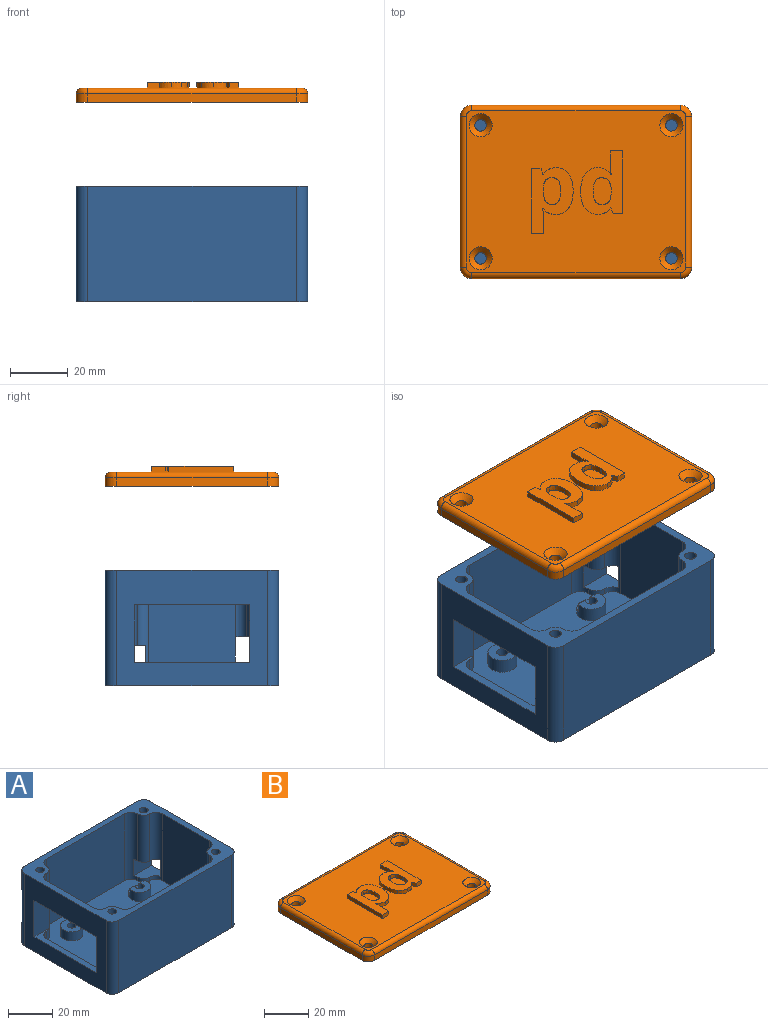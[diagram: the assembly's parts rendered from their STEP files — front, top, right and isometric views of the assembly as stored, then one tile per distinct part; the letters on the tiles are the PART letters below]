
ASSEMBLY  parts=2 mates=1
PART A: 74 faces, bbox 80x60x40 mm
  f0: plane 30x12mm, normal (1,0,0), area 360mm2, adj f3,f5,f16,f66
  f1: plane 52x40mm, normal (-1,0,0), area 1280mm2, adj f16,f19,f66,f67,f68,f69,f70,f71
  f2: cylinder r=4mm len=37mm, axis (0,0,1), area 174.7mm2, adj f5,f11,f16,f27,f33,f66,f67,f68
  f3: cylinder r=4mm len=12mm, axis (0,0,-1), area 75.4mm2, adj f0,f4,f16,f66
  f4: cylinder r=4mm len=37mm, axis (0,0,1), area 174.7mm2, adj f3,f11,f16,f28,f29,f66,f68,f69
  f5: cylinder r=4mm len=12mm, axis (0,0,1), area 75.4mm2, adj f0,f2,f16,f66
  f6: plane 52x40mm, normal (1,0,0), area 1879mm2, adj f16,f19,f58,f59,f60,f61,f62,f63
  f7: cylinder r=4mm len=4mm, axis (0,0,1), area 12.6mm2, adj f11,f30,f32,f64
  f8: cylinder r=4mm len=4mm, axis (0,0,-1), area 12.6mm2, adj f9,f11,f13,f60
  f9: cylinder r=4mm len=4mm, axis (0,0,1), area 12.6mm2, adj f8,f10,f11,f60
  f10: cylinder r=4mm len=37mm, axis (0,0,-1), area 207.3mm2, adj f9,f11,f12,f16,f35,f58,f59,f60
  f11: plane 74x54mm, normal (0,0,1), area 3412.1mm2, adj f2,f4,f7,f8,f9,f10,f12,f13
  f12: plane 50x37mm, normal (0,1,0), area 1850mm2, adj f10,f11,f16,f28
  f13: plane 37x30mm, normal (-1,0,0), area 1110mm2, adj f8,f11,f16,f32,f34,f61
  f14: plane 50x37mm, normal (0,-1,0), area 1850mm2, adj f11,f16,f27,f30
  f15: plane 30x5mm, normal (1,0,0), area 150mm2, adj f11,f29,f33,f68
  f16: plane 80x60mm, normal (0,0,1), area 1009.7mm2, adj f0,f1,f2,f3,f4,f5,f6,f10
  f17: plane 72x40mm, normal (0,1,0), area 2880mm2, adj f16,f19,f70,f73
  f18: plane 72x40mm, normal (0,-1,0), area 2880mm2, adj f16,f19,f71,f72
  f19: plane 80x60mm, normal (0,0,-1), area 4786.3mm2, adj f1,f6,f17,f18,f70,f71,f72,f73
  f20: cylinder r=2mm len=25mm, axis (0,0,1), area 314.2mm2, adj f16,f21
  f21: plane 4x4mm, normal (0,0,1), area 12.6mm2, adj f20
  f22: cylinder r=2mm len=25mm, axis (0,0,1), area 314.2mm2, adj f16,f23
  f23: plane 4x4mm, normal (0,0,1), area 12.6mm2, adj f22
  f24: cylinder r=2mm len=23mm, axis (0,0,1), area 289mm2, adj f16,f58
  f25: cylinder r=2mm len=25mm, axis (0,0,1), area 314.2mm2, adj f16,f26
  f26: plane 4x4mm, normal (0,0,1), area 12.6mm2, adj f25
  f27: cylinder r=4mm len=37mm, axis (0,0,1), area 232.5mm2, adj f2,f11,f14,f16
  f28: cylinder r=4mm len=37mm, axis (0,0,1), area 232.5mm2, adj f4,f11,f12,f16
  f29: cylinder r=4mm len=5mm, axis (0,0,-1), area 31.4mm2, adj f4,f11,f15,f68
  f30: cylinder r=4mm len=37mm, axis (0,0,-1), area 213.6mm2, adj f7,f11,f14,f16,f31,f62,f63,f64
  f31: cylinder r=4mm len=26mm, axis (0,0,1), area 163.4mm2, adj f16,f30,f32,f63
  f32: cylinder r=4mm len=37mm, axis (0,0,1), area 185mm2, adj f7,f11,f13,f16,f31,f63,f64,f65
  f33: cylinder r=4mm len=5mm, axis (0,0,1), area 31.4mm2, adj f2,f11,f15,f68
  f34: cylinder r=4mm len=23mm, axis (0,0,-1), area 144.5mm2, adj f13,f16,f35,f58
  f35: cylinder r=4mm len=23mm, axis (0,0,1), area 144.5mm2, adj f10,f16,f34,f58
  f36: cylinder r=2mm len=5mm, axis (0,0,-1), area 62.8mm2, adj f38,f39
  f37: cylinder r=5mm len=10mm, axis (0,0,-1), area 157.1mm2, adj f11,f38
  f38: plane 10x10mm, normal (0,0,1), area 66mm2, adj f36,f37
  f39: plane 4x4mm, normal (0,0,1), area 12.6mm2, adj f36
  f40: cylinder r=5mm len=10mm, axis (0,0,-1), area 120.8mm2, adj f11,f42,f55,f56,f57
  f41: cylinder r=2mm len=5mm, axis (0,0,-1), area 56.9mm2, adj f42,f43,f55,f56,f57
  f42: plane 10x6.76mm, normal (0,0,1), area 44.2mm2, adj f40,f41,f55,f56
  f43: plane 4x4mm, normal (0,0,1), area 12.6mm2, adj f41
  f44: cylinder r=2mm len=5mm, axis (0,0,-1), area 48.7mm2, adj f46,f47,f52,f53,f54
  f45: cylinder r=5mm len=10mm, axis (0,0,-1), area 114.5mm2, adj f11,f46,f52,f53,f54
  f46: plane 10x5.76mm, normal (0,0,1), area 37.6mm2, adj f44,f45,f52,f53
  f47: plane 4x4mm, normal (0,0,1), area 12.6mm2, adj f44
  f48: cylinder r=5mm len=10mm, axis (0,0,-1), area 157.1mm2, adj f11,f50
  f49: cylinder r=2mm len=5mm, axis (0,0,-1), area 62.8mm2, adj f50,f51
  f50: plane 10x10mm, normal (0,0,1), area 66mm2, adj f48,f49
  f51: plane 4x4mm, normal (0,0,1), area 12.6mm2, adj f49
  f52: plane 3.09x3mm, normal (0,-1,0), area 9.3mm2, adj f44,f45,f46,f54
  f53: plane 3.09x3mm, normal (0,-1,0), area 9.3mm2, adj f44,f45,f46,f54
  f54: plane 9.88x4.24mm, normal (0,0,1), area 28.4mm2, adj f44,f45,f52,f53
  f55: plane 3.73x3mm, normal (0,1,0), area 11.2mm2, adj f40,f41,f42,f57
  f56: plane 3.73x3mm, normal (0,1,0), area 11.2mm2, adj f40,f41,f42,f57
  f57: plane 9.36x3.24mm, normal (0,0,1), area 21.7mm2, adj f40,f41,f55,f56
  f58: plane 11.54x10mm, normal (0,0,-1), area 65.8mm2, adj f6,f10,f24,f34,f35,f59,f61
  f59: plane 12x11.54mm, normal (0,1,0), area 138.4mm2, adj f6,f10,f58,f60
  f60: plane 11.54x10mm, normal (0,0,1), area 78.3mm2, adj f6,f8,f9,f10,f59,f61
  f61: plane 12x3mm, normal (0,-1,0), area 36mm2, adj f6,f13,f58,f60
  f62: plane 11.54x9mm, normal (0,-1,0), area 103.8mm2, adj f6,f30,f63,f64
  f63: plane 11.54x9mm, normal (0,0,-1), area 75.3mm2, adj f6,f30,f31,f32,f62,f65
  f64: plane 11.54x9mm, normal (0,0,1), area 75.3mm2, adj f6,f7,f30,f32,f62,f65
  f65: plane 9x3.13mm, normal (0,1,0), area 28.1mm2, adj f6,f32,f63,f64
  f66: plane 40x9.65mm, normal (0,0,-1), area 138.5mm2, adj f0,f1,f2,f3,f4,f5,f67,f69
  f67: plane 20x9.65mm, normal (0,-1,0), area 192.9mm2, adj f1,f2,f66,f68
  f68: plane 40x9.65mm, normal (0,0,1), area 138.5mm2, adj f1,f2,f4,f15,f29,f33,f67,f69
  f69: plane 20x9.65mm, normal (0,1,0), area 192.9mm2, adj f1,f4,f66,f68
  f70: cylinder r=4mm len=40mm, axis (0,0,1), area 251.3mm2, adj f1,f16,f17,f19
  f71: cylinder r=4mm len=40mm, axis (0,0,-1), area 251.3mm2, adj f1,f16,f18,f19
  f72: cylinder r=4mm len=40mm, axis (0,0,1), area 251.3mm2, adj f6,f16,f18,f19
  f73: cylinder r=4mm len=40mm, axis (0,0,-1), area 251.3mm2, adj f6,f16,f17,f19
PART B: 76 faces, bbox 80.7x60.7x7 mm
  f0: plane 76x56mm, normal (0,0,1), area 3579.2mm2, adj f10,f11,f12,f13,f14,f15,f16,f17
  f1: plane 72x3mm, normal (0,1,0), area 216mm2, adj f5,f14,f72,f74
  f2: plane 52x3mm, normal (-1,0,0), area 156mm2, adj f5,f15,f70,f72
  f3: plane 72x3mm, normal (0,-1,0), area 216mm2, adj f5,f17,f68,f70
  f4: plane 52x3mm, normal (1,0,0), area 156mm2, adj f5,f16,f68,f74
  f5: plane 80x60mm, normal (0,0,-1), area 4736mm2, adj f1,f2,f3,f4,f6,f7,f8,f9
  f6: cylinder r=2mm len=4mm, axis (0,0,1), area 37.7mm2, adj f5,f11
  f7: cylinder r=2mm len=4mm, axis (0,0,1), area 37.7mm2, adj f5,f10
  f8: cylinder r=2mm len=4mm, axis (0,0,1), area 37.7mm2, adj f5,f13
  f9: cylinder r=2mm len=4mm, axis (0,0,1), area 37.7mm2, adj f5,f12
  f10: cone r=2mm half-angle=45deg, axis (0,0,1), area 53.3mm2, adj f0,f7
  f11: cone r=2mm half-angle=45deg, axis (0,0,1), area 53.3mm2, adj f0,f6
  f12: cone r=2mm half-angle=45deg, axis (0,0,1), area 53.3mm2, adj f0,f9
  f13: cone r=2mm half-angle=45deg, axis (0,0,1), area 53.3mm2, adj f0,f8
  f14: cylinder r=2mm len=72mm, axis (1,0,0), area 226.2mm2, adj f0,f1,f73,f75
  f15: cylinder r=2mm len=52mm, axis (0,1,0), area 163.4mm2, adj f0,f2,f71,f73
  f16: cylinder r=2mm len=52mm, axis (0,-1,0), area 163.4mm2, adj f0,f4,f69,f75
  f17: cylinder r=2mm len=72mm, axis (-1,0,0), area 226.2mm2, adj f0,f3,f69,f71
  f18: extruded ~2.3x2mm, area 5.2mm2, adj f19,f40,f41,f42
  f19: extruded ~2.21x2mm, area 5.2mm2, adj f18,f20,f41,f42
  f20: extruded ~3.45x2mm, area 7.1mm2, adj f19,f21,f41,f42
  f21: extruded ~4.72x2.86mm, area 12.4mm2, adj f20,f22,f41,f42
  f22: extruded ~2.36x2mm, area 5.4mm2, adj f21,f23,f41,f42
  f23: extruded ~3.6x2mm, area 7.4mm2, adj f22,f24,f41,f42
  f24: plane 2x0.46mm, normal (1,0,0), area 0.9mm2, adj f23,f40,f41,f42
  f25: extruded ~4.31x2mm, area 9.9mm2, adj f0,f26,f39,f41
  f26: extruded ~3.18x2mm, area 6.7mm2, adj f0,f25,f27,f41
  f27: extruded ~2.8x2.09mm, area 7.1mm2, adj f0,f26,f28,f41
  f28: extruded ~4.33x2mm, area 8.8mm2, adj f0,f27,f29,f41
  f29: extruded ~5.92x2mm, area 12.5mm2, adj f0,f28,f30,f41
  f30: extruded ~4.32x2.13mm, area 10mm2, adj f0,f29,f31,f41
  f31: extruded ~4.42x2.31mm, area 10.4mm2, adj f0,f30,f32,f41
  f32: plane 2x0.2mm, normal (0,1,0), area 0.4mm2, adj f0,f31,f33,f41
  f33: plane 2.02x2mm, normal (0.96,0.28,0), area 4.2mm2, adj f0,f32,f34,f41
  f34: plane 3.46x2mm, normal (0,1,0), area 6.9mm2, adj f0,f33,f35,f41
  f35: plane 22.45x2mm, normal (-1,0,0), area 44.9mm2, adj f0,f34,f36,f41
  f36: plane 4.25x2mm, normal (0,-1,0), area 8.5mm2, adj f0,f35,f37,f41
  f37: plane 6.32x2mm, normal (1,0,0), area 12.6mm2, adj f0,f36,f38,f41
  f38: extruded ~2.26x2mm, area 4.5mm2, adj f0,f37,f39,f41
  f39: plane 2x0.22mm, normal (0,-1,0), area 0.4mm2, adj f0,f25,f38,f41
  f40: extruded ~3.2x2mm, area 6.7mm2, adj f18,f24,f41,f42
  f41: plane 22.74x14.56mm, normal (0,0,1), area 190.8mm2, adj f18,f19,f20,f21,f22,f23,f24,f25
  f42: plane 9.31x5.97mm, normal (0,0,1), area 46.9mm2, adj f18,f19,f20,f21,f22,f23,f24,f40
  f43: extruded ~2.39x2mm, area 5.3mm2, adj f44,f65,f66,f67
  f44: extruded ~2.28x2mm, area 5.3mm2, adj f43,f45,f66,f67
  f45: extruded ~3.45x2mm, area 7.2mm2, adj f44,f46,f66,f67
  f46: extruded ~3.51x2mm, area 7.3mm2, adj f45,f47,f66,f67
  f47: extruded ~2.21x2mm, area 5.3mm2, adj f46,f48,f66,f67
  f48: extruded ~2.52x2mm, area 5.7mm2, adj f47,f49,f66,f67
  f49: extruded ~3.6x2mm, area 7.5mm2, adj f48,f50,f66,f67
  f50: plane 2x0.46mm, normal (-1,0,0), area 0.9mm2, adj f49,f65,f66,f67
  f51: extruded ~4.31x2.13mm, area 10mm2, adj f0,f52,f64,f66
  f52: extruded ~4.42x2.3mm, area 10.5mm2, adj f0,f51,f53,f66
  f53: plane 2x0.18mm, normal (0,-1,0), area 0.4mm2, adj f0,f52,f54,f66
  f54: plane 2.02x2mm, normal (-0.93,-0.38,0), area 4.4mm2, adj f0,f53,f55,f66
  f55: plane 3.26x2mm, normal (0,-1,0), area 6.5mm2, adj f0,f54,f56,f66
  f56: plane 21.69x2mm, normal (1,0,0), area 43.4mm2, adj f0,f55,f57,f66
  f57: plane 4.26x2mm, normal (0,1,0), area 8.5mm2, adj f0,f56,f58,f66
  f58: plane 4.99x2mm, normal (-1,0,0), area 10mm2, adj f0,f57,f59,f66
  f59: extruded ~3.11x2mm, area 6.3mm2, adj f0,f58,f60,f66
  f60: plane 2x0.14mm, normal (0,1,0), area 0.3mm2, adj f0,f59,f61,f66
  f61: extruded ~4.49x2.28mm, area 10.5mm2, adj f0,f60,f62,f66
  f62: extruded ~4.4x2.14mm, area 10.2mm2, adj f0,f61,f63,f66
  f63: extruded ~5.97x2mm, area 12.6mm2, adj f0,f62,f64,f66
  f64: extruded ~5.91x2mm, area 12.4mm2, adj f0,f51,f63,f66
  f65: extruded ~3.22x2mm, area 6.8mm2, adj f43,f50,f66,f67
  f66: plane 21.97x14.57mm, normal (0,0,1), area 185.5mm2, adj f43,f44,f45,f46,f47,f48,f49,f50
  f67: plane 9.31x6.29mm, normal (0,0,1), area 49.1mm2, adj f43,f44,f45,f46,f47,f48,f49,f50
  f68: cylinder r=4mm len=4mm, axis (0,0,1), area 18.8mm2, adj f3,f4,f5,f69
  f69: torus R=2mm, axis (0,0,1), area 16.2mm2, adj f0,f16,f17,f68
  f70: cylinder r=4mm len=4mm, axis (0,0,-1), area 18.8mm2, adj f2,f3,f5,f71
  f71: torus R=2mm, axis (0,0,1), area 16.2mm2, adj f0,f15,f17,f70
  f72: cylinder r=4mm len=4mm, axis (0,0,1), area 18.8mm2, adj f1,f2,f5,f73
  f73: torus R=2mm, axis (0,0,1), area 16.2mm2, adj f0,f14,f15,f72
  f74: cylinder r=4mm len=4mm, axis (0,0,-1), area 18.8mm2, adj f1,f4,f5,f75
  f75: torus R=2mm, axis (0,0,1), area 16.2mm2, adj f0,f14,f16,f74
PLACE A t=(24.29,-44.64,-19.82)mm fixed
PLACE B t=(8.25,-26.23,49.07)mm
MATE slider A.f9 <-> B.f9  axis (0,0,1) through (22.12,-29.17,20.18)mm
